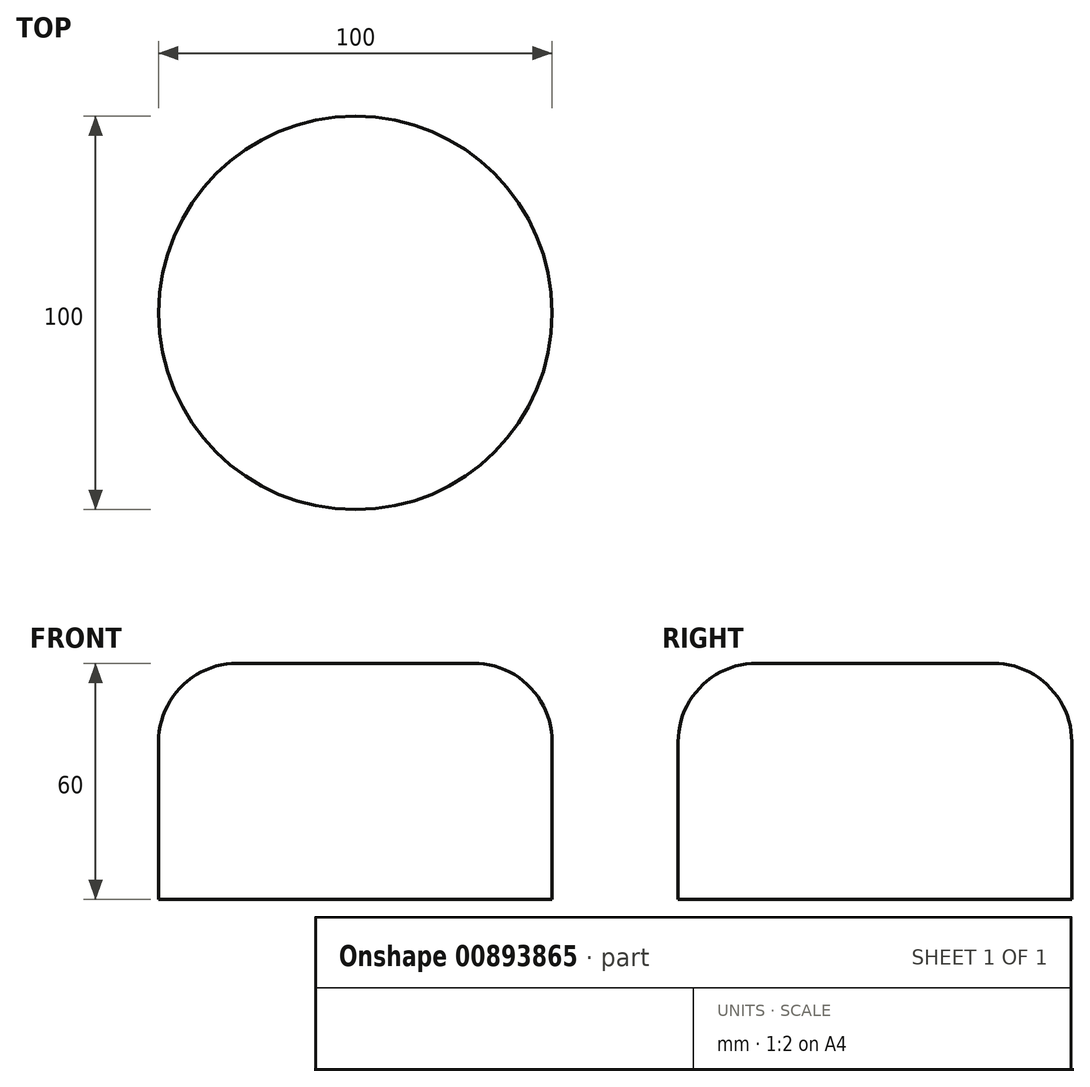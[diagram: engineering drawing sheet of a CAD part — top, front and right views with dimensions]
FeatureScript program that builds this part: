
annotation { "Feature Type Name" : "Feature", "Feature Type Description" : "" }
export const myFeature = defineFeature(function(context is Context, id is Id, definition is map)
    precondition{}
    {
        {
            var Q0;
            Q0=qCreatedBy(makeId("Top.planeOp"),FACE);
            var sketch = newSketch(context, id + "F0", { "sketchPlane" : qUnion([Q0])});
            skCircle(sketch, "E0", {"center": v(0, 0) * mm, "radius": 50 * mm});
            skLineSegment(sketch, "E1", {"start": v(24.44, 43.62) * mm, "end": v(-24.44, 43.62) * mm});
            skSolve(sketch);
        }
        {
            var Q0;
            Q0=makeQuery(id+"F0.imprint","IMPRINT",FACE,{"disambiguationData":[TD([[makeQuery(id+"F0.imprint","IMPRINT",EDGE,{"derivedFrom":sQuery(id+"F0.wireOp",EDGE,"E0")}),1.0]])]});
            extrude(context, id + "F1", {"entities" : qUnion([Q0]), "depth" : 60 * mm, "offsetDistance" : 25 * mm});
        }
        {
            var Q0;
            Q0=makeQuery(id+"F1.opExtrude","CAP_EDGE",EDGE,{"disambiguationData":[OSD([sQuery(id+"F0.wireOp",EDGE,"E0")])],"isStart":false});
            fillet(context, id + "F2", {"entities" : qUnion([Q0]), "radius" : 20 * mm, "tangentPropagation" : true, "allowEdgeOverflow" : false});
        }
    });
